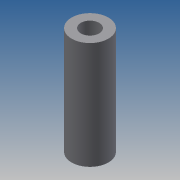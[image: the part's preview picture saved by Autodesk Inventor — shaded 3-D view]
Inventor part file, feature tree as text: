
AUTODESK INVENTOR PART (.ipt)
format: ipt  version: 2013 (Build 170138000, 138)  size: 69,632 bytes
history: native  units: mm
features: extrude x1, sketch x1
ambient origin geometry x8: Origin, YZ Plane, XZ Plane, XY Plane, X Axis, Y Axis, Z Axis, Center Point
bodies: Solid1 (feature_tree)
feature tree (2):
  extrude  "Extrusion1"  Depth=6.0mm
  sketch  "Sketch1"  dims[d0=12.0mm d2=6.0mm d3=35.0mm d4=0.0mm]
